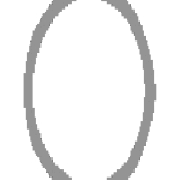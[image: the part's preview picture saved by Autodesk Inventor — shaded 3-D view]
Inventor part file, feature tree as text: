
AUTODESK INVENTOR PART (.ipt)
format: ipt  version: 2021 (Build 250183000, 183)  size: 110,080 bytes
history: native  units: in
note: dims shown in document units (in); Inventor stores cm internally (conversion verified against a paired STEP export)
features: other x4, sketch x3, plane x1
ambient origin geometry x8: Origin, YZ Plane, XZ Plane, XY Plane, X Axis, Y Axis, Z Axis, Center Point
bodies: Solid1 (feature_tree), Body (feature_tree)
feature tree (8):
  other  "Driven Length"
  other  "Frame Generator"
  other  "Start Plane"
  other  "End Plane"
  sketch  "Sketch"  dims[d2=14.0674in d4=-0.0in d5=14.0674in d6=0.12in d7=0.0in d8=90.0deg d9=14.0674in]
  sketch  "Sketch2"  dims[d0=1.0in]
  plane  "Work Plane3"
  sketch  "Sketch3"  dims[d1=0.065in]
